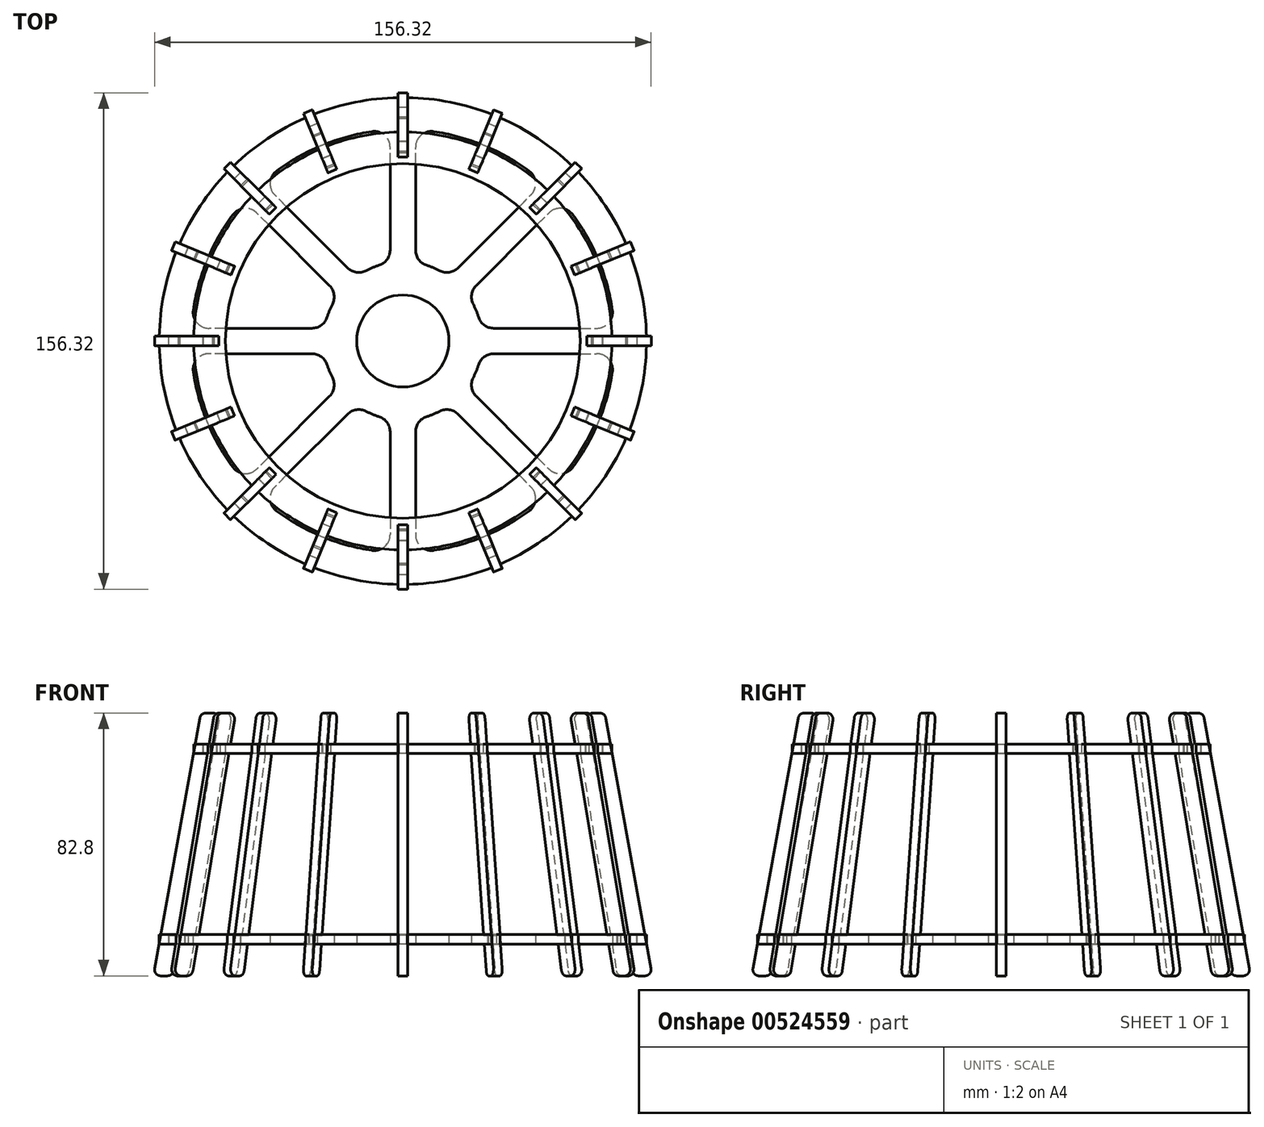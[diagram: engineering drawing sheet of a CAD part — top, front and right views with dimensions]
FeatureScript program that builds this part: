
annotation { "Feature Type Name" : "Feature", "Feature Type Description" : "" }
export const myFeature = defineFeature(function(context is Context, id is Id, definition is map)
    precondition{}
    {
        {
            var Q0;
            Q0=qCreatedBy(makeId("Top.planeOp"),FACE);
            cPlane(context, id + "F0", {"entities" : qUnion([Q0]), "cplaneType" : CPlaneType.OFFSET, "offset" : 60 * mm, "oppositeDirection" : true, "width" : 150 * mm, "height" : 150 * mm});
        }
        {
            var Q0;
            Q0=qCreatedBy(makeId("Top.planeOp"),FACE);
            var sketch = newSketch(context, id + "F1", { "sketchPlane" : qUnion([Q0])});
            skCircle(sketch, "E0", {"center": v(0, 0) * mm, "radius": 55.83 * mm});
            skArc(sketch, "E1", {"start": v(-65.82, -1.4) * mm, "mid": v(-64.57, -12.84) * mm, "end": v(-61.34, -23.9) * mm});
            skLineSegment(sketch, "E2", {"start": v(-65.82, 1.4) * mm, "end": v(-62.82, 1.4) * mm});
            skLineSegment(sketch, "E3", {"start": v(-62.82, 1.4) * mm, "end": v(-62.82, -1.4) * mm});
            skLineSegment(sketch, "E4", {"start": v(-62.82, -1.4) * mm, "end": v(-65.82, -1.4) * mm});
            skLineSegment(sketch, "E5.1.0", {"start": v(-61.34, -23.9) * mm, "end": v(-58.57, -22.75) * mm});
            skLineSegment(sketch, "E5.1.1", {"start": v(-58.57, -22.75) * mm, "end": v(-57.5, -25.33) * mm});
            skLineSegment(sketch, "E5.1.2", {"start": v(-57.5, -25.33) * mm, "end": v(-60.27, -26.48) * mm});
            skLineSegment(sketch, "E5.2.0", {"start": v(-47.53, -45.55) * mm, "end": v(-45.4, -43.43) * mm});
            skLineSegment(sketch, "E5.2.1", {"start": v(-45.4, -43.43) * mm, "end": v(-43.43, -45.4) * mm});
            skLineSegment(sketch, "E5.2.2", {"start": v(-43.43, -45.4) * mm, "end": v(-45.55, -47.53) * mm});
            skLineSegment(sketch, "E5.3.0", {"start": v(-26.48, -60.27) * mm, "end": v(-25.33, -57.5) * mm});
            skLineSegment(sketch, "E5.3.1", {"start": v(-25.33, -57.5) * mm, "end": v(-22.75, -58.57) * mm});
            skLineSegment(sketch, "E5.3.2", {"start": v(-22.75, -58.57) * mm, "end": v(-23.9, -61.34) * mm});
            skLineSegment(sketch, "E5.4.0", {"start": v(-1.4, -65.82) * mm, "end": v(-1.4, -62.82) * mm});
            skLineSegment(sketch, "E5.4.1", {"start": v(-1.4, -62.82) * mm, "end": v(1.4, -62.82) * mm});
            skLineSegment(sketch, "E5.4.2", {"start": v(1.4, -62.82) * mm, "end": v(1.4, -65.82) * mm});
            skLineSegment(sketch, "E5.5.0", {"start": v(23.9, -61.34) * mm, "end": v(22.75, -58.57) * mm});
            skLineSegment(sketch, "E5.5.1", {"start": v(22.75, -58.57) * mm, "end": v(25.33, -57.5) * mm});
            skLineSegment(sketch, "E5.5.2", {"start": v(25.33, -57.5) * mm, "end": v(26.48, -60.27) * mm});
            skLineSegment(sketch, "E5.6.0", {"start": v(45.55, -47.53) * mm, "end": v(43.43, -45.4) * mm});
            skLineSegment(sketch, "E5.6.1", {"start": v(43.43, -45.4) * mm, "end": v(45.4, -43.43) * mm});
            skLineSegment(sketch, "E5.6.2", {"start": v(45.4, -43.43) * mm, "end": v(47.53, -45.55) * mm});
            skLineSegment(sketch, "E5.7.0", {"start": v(60.27, -26.48) * mm, "end": v(57.5, -25.33) * mm});
            skLineSegment(sketch, "E5.7.1", {"start": v(57.5, -25.33) * mm, "end": v(58.57, -22.75) * mm});
            skLineSegment(sketch, "E5.7.2", {"start": v(58.57, -22.75) * mm, "end": v(61.34, -23.9) * mm});
            skLineSegment(sketch, "E5.8.0", {"start": v(65.82, -1.4) * mm, "end": v(62.82, -1.4) * mm});
            skLineSegment(sketch, "E5.8.1", {"start": v(62.82, -1.4) * mm, "end": v(62.82, 1.4) * mm});
            skLineSegment(sketch, "E5.8.2", {"start": v(62.82, 1.4) * mm, "end": v(65.82, 1.4) * mm});
            skLineSegment(sketch, "E5.9.0", {"start": v(61.34, 23.9) * mm, "end": v(58.57, 22.75) * mm});
            skLineSegment(sketch, "E5.9.1", {"start": v(58.57, 22.75) * mm, "end": v(57.5, 25.33) * mm});
            skLineSegment(sketch, "E5.9.2", {"start": v(57.5, 25.33) * mm, "end": v(60.27, 26.48) * mm});
            skLineSegment(sketch, "E5.10.0", {"start": v(47.53, 45.55) * mm, "end": v(45.4, 43.43) * mm});
            skLineSegment(sketch, "E5.10.1", {"start": v(45.4, 43.43) * mm, "end": v(43.43, 45.4) * mm});
            skLineSegment(sketch, "E5.10.2", {"start": v(43.43, 45.4) * mm, "end": v(45.55, 47.53) * mm});
            skLineSegment(sketch, "E5.11.0", {"start": v(26.48, 60.27) * mm, "end": v(25.33, 57.5) * mm});
            skLineSegment(sketch, "E5.11.1", {"start": v(25.33, 57.5) * mm, "end": v(22.75, 58.57) * mm});
            skLineSegment(sketch, "E5.11.2", {"start": v(22.75, 58.57) * mm, "end": v(23.9, 61.34) * mm});
            skLineSegment(sketch, "E5.12.0", {"start": v(1.4, 65.82) * mm, "end": v(1.4, 62.82) * mm});
            skLineSegment(sketch, "E5.12.1", {"start": v(1.4, 62.82) * mm, "end": v(-1.4, 62.82) * mm});
            skLineSegment(sketch, "E5.12.2", {"start": v(-1.4, 62.82) * mm, "end": v(-1.4, 65.82) * mm});
            skLineSegment(sketch, "E5.13.0", {"start": v(-23.9, 61.34) * mm, "end": v(-22.75, 58.57) * mm});
            skLineSegment(sketch, "E5.13.1", {"start": v(-22.75, 58.57) * mm, "end": v(-25.33, 57.5) * mm});
            skLineSegment(sketch, "E5.13.2", {"start": v(-25.33, 57.5) * mm, "end": v(-26.48, 60.27) * mm});
            skLineSegment(sketch, "E5.14.0", {"start": v(-45.55, 47.53) * mm, "end": v(-43.43, 45.4) * mm});
            skLineSegment(sketch, "E5.14.1", {"start": v(-43.43, 45.4) * mm, "end": v(-45.4, 43.43) * mm});
            skLineSegment(sketch, "E5.14.2", {"start": v(-45.4, 43.43) * mm, "end": v(-47.53, 45.55) * mm});
            skLineSegment(sketch, "E5.15.0", {"start": v(-60.27, 26.48) * mm, "end": v(-57.5, 25.33) * mm});
            skLineSegment(sketch, "E5.15.1", {"start": v(-57.5, 25.33) * mm, "end": v(-58.57, 22.75) * mm});
            skLineSegment(sketch, "E5.15.2", {"start": v(-58.57, 22.75) * mm, "end": v(-61.34, 23.9) * mm});
            skArc(sketch, "E6.trimOffspring", {"start": v(-61.34, 23.9) * mm, "mid": v(-64.57, 12.84) * mm, "end": v(-65.82, 1.4) * mm});
            skArc(sketch, "E7.trimOffspring", {"start": v(-47.53, 45.55) * mm, "mid": v(-54.74, 36.57) * mm, "end": v(-60.27, 26.48) * mm});
            skArc(sketch, "E8.trimOffspring", {"start": v(-26.48, 60.27) * mm, "mid": v(-36.57, 54.74) * mm, "end": v(-45.55, 47.53) * mm});
            skArc(sketch, "E9.trimOffspring", {"start": v(-1.4, 65.82) * mm, "mid": v(-12.84, 64.57) * mm, "end": v(-23.9, 61.34) * mm});
            skArc(sketch, "E10.trimOffspring", {"start": v(23.9, 61.34) * mm, "mid": v(12.84, 64.57) * mm, "end": v(1.4, 65.82) * mm});
            skArc(sketch, "E11.trimOffspring", {"start": v(45.55, 47.53) * mm, "mid": v(36.57, 54.74) * mm, "end": v(26.48, 60.27) * mm});
            skArc(sketch, "E12.trimOffspring", {"start": v(60.27, 26.48) * mm, "mid": v(54.74, 36.57) * mm, "end": v(47.53, 45.55) * mm});
            skArc(sketch, "E13.trimOffspring", {"start": v(65.82, 1.4) * mm, "mid": v(64.57, 12.84) * mm, "end": v(61.34, 23.9) * mm});
            skArc(sketch, "E14.trimOffspring", {"start": v(61.34, -23.9) * mm, "mid": v(64.57, -12.84) * mm, "end": v(65.82, -1.4) * mm});
            skArc(sketch, "E15.trimOffspring", {"start": v(47.53, -45.55) * mm, "mid": v(54.74, -36.57) * mm, "end": v(60.27, -26.48) * mm});
            skArc(sketch, "E16.trimOffspring", {"start": v(26.48, -60.27) * mm, "mid": v(36.57, -54.74) * mm, "end": v(45.55, -47.53) * mm});
            skArc(sketch, "E17.trimOffspring", {"start": v(1.4, -65.82) * mm, "mid": v(12.84, -64.57) * mm, "end": v(23.9, -61.34) * mm});
            skArc(sketch, "E18.trimOffspring", {"start": v(-23.9, -61.34) * mm, "mid": v(-12.84, -64.57) * mm, "end": v(-1.4, -65.82) * mm});
            skArc(sketch, "E19.trimOffspring", {"start": v(-45.55, -47.53) * mm, "mid": v(-36.57, -54.74) * mm, "end": v(-26.48, -60.27) * mm});
            skArc(sketch, "E20.trimOffspring", {"start": v(-60.27, -26.48) * mm, "mid": v(-54.74, -36.57) * mm, "end": v(-47.53, -45.55) * mm});
            skSolve(sketch);
        }
        {
            var Q0;
            Q0=qSketchRegion(id+"F1",true);
            extrude(context, id + "F2", {"entities" : qUnion([Q0]), "depth" : 3 * mm});
        }
        {
            var Q0;
            Q0=qCreatedBy(id+"F0.planeOp",FACE);
            var sketch = newSketch(context, id + "F3", { "sketchPlane" : qUnion([Q0])});
            skArc(sketch, "E21", {"start": v(-9.73, 65.95) * mm, "mid": v(-25.51, 61.6) * mm, "end": v(-39.76, 53.52) * mm});
            skArc(sketch, "E22", {"start": v(-76.65, -1.4) * mm, "mid": v(-75.2, -14.96) * mm, "end": v(-71.36, -28.04) * mm});
            skArc(sketch, "E23.trimOffspring", {"start": v(-71.36, 28.04) * mm, "mid": v(-75.2, 14.96) * mm, "end": v(-76.65, 1.4) * mm});
            skArc(sketch, "E24.trimOffspring", {"start": v(-55.2, 53.21) * mm, "mid": v(-63.75, 42.6) * mm, "end": v(-70.28, 30.63) * mm});
            skArc(sketch, "E25.trimOffspring", {"start": v(-30.63, 70.28) * mm, "mid": v(-42.6, 63.75) * mm, "end": v(-53.21, 55.2) * mm});
            skArc(sketch, "E26.trimOffspring", {"start": v(-1.4, 76.65) * mm, "mid": v(-14.96, 75.2) * mm, "end": v(-28.04, 71.36) * mm});
            skArc(sketch, "E27.trimOffspring", {"start": v(28.04, 71.36) * mm, "mid": v(14.96, 75.2) * mm, "end": v(1.4, 76.65) * mm});
            skArc(sketch, "E28.trimOffspring", {"start": v(53.21, 55.2) * mm, "mid": v(42.6, 63.75) * mm, "end": v(30.63, 70.28) * mm});
            skArc(sketch, "E29.trimOffspring", {"start": v(70.28, 30.63) * mm, "mid": v(63.75, 42.6) * mm, "end": v(55.2, 53.21) * mm});
            skArc(sketch, "E30.trimOffspring", {"start": v(76.65, 1.4) * mm, "mid": v(75.2, 14.96) * mm, "end": v(71.36, 28.04) * mm});
            skArc(sketch, "E31.trimOffspring", {"start": v(71.36, -28.04) * mm, "mid": v(75.2, -14.96) * mm, "end": v(76.65, -1.4) * mm});
            skArc(sketch, "E32.trimOffspring", {"start": v(55.2, -53.21) * mm, "mid": v(63.75, -42.6) * mm, "end": v(70.28, -30.63) * mm});
            skArc(sketch, "E33.trimOffspring", {"start": v(30.63, -70.28) * mm, "mid": v(42.6, -63.75) * mm, "end": v(53.21, -55.2) * mm});
            skArc(sketch, "E34.trimOffspring", {"start": v(1.4, -76.65) * mm, "mid": v(14.96, -75.2) * mm, "end": v(28.04, -71.36) * mm});
            skArc(sketch, "E35.trimOffspring", {"start": v(-28.04, -71.36) * mm, "mid": v(-14.96, -75.2) * mm, "end": v(-1.4, -76.65) * mm});
            skArc(sketch, "E36.trimOffspring", {"start": v(-53.21, -55.2) * mm, "mid": v(-42.6, -63.75) * mm, "end": v(-30.63, -70.28) * mm});
            skArc(sketch, "E37.trimOffspring", {"start": v(-70.28, -30.63) * mm, "mid": v(-63.75, -42.6) * mm, "end": v(-55.2, -53.21) * mm});
            skLineSegment(sketch, "E38", {"start": v(-76.65, -1.4) * mm, "end": v(-73.65, -1.4) * mm});
            skLineSegment(sketch, "E39", {"start": v(-73.65, -1.4) * mm, "end": v(-73.65, 1.4) * mm});
            skLineSegment(sketch, "E40", {"start": v(-76.65, 1.4) * mm, "end": v(-73.65, 1.4) * mm});
            skLineSegment(sketch, "E41.1.0", {"start": v(-71.36, -28.04) * mm, "end": v(-68.58, -26.9) * mm});
            skLineSegment(sketch, "E41.1.1", {"start": v(-67.51, -29.48) * mm, "end": v(-68.58, -26.9) * mm});
            skLineSegment(sketch, "E41.1.2", {"start": v(-70.28, -30.63) * mm, "end": v(-67.51, -29.48) * mm});
            skLineSegment(sketch, "E41.2.0", {"start": v(-55.2, -53.21) * mm, "end": v(-53.07, -51.1) * mm});
            skLineSegment(sketch, "E41.2.1", {"start": v(-51.1, -53.07) * mm, "end": v(-53.07, -51.1) * mm});
            skLineSegment(sketch, "E41.2.2", {"start": v(-53.21, -55.2) * mm, "end": v(-51.1, -53.07) * mm});
            skLineSegment(sketch, "E41.3.0", {"start": v(-30.63, -70.28) * mm, "end": v(-29.48, -67.51) * mm});
            skLineSegment(sketch, "E41.3.1", {"start": v(-26.9, -68.58) * mm, "end": v(-29.48, -67.51) * mm});
            skLineSegment(sketch, "E41.3.2", {"start": v(-28.04, -71.36) * mm, "end": v(-26.9, -68.58) * mm});
            skLineSegment(sketch, "E41.4.0", {"start": v(-1.4, -76.65) * mm, "end": v(-1.4, -73.65) * mm});
            skLineSegment(sketch, "E41.4.1", {"start": v(1.4, -73.65) * mm, "end": v(-1.4, -73.65) * mm});
            skLineSegment(sketch, "E41.4.2", {"start": v(1.4, -76.65) * mm, "end": v(1.4, -73.65) * mm});
            skLineSegment(sketch, "E41.5.0", {"start": v(28.04, -71.36) * mm, "end": v(26.9, -68.58) * mm});
            skLineSegment(sketch, "E41.5.1", {"start": v(29.48, -67.51) * mm, "end": v(26.9, -68.58) * mm});
            skLineSegment(sketch, "E41.5.2", {"start": v(30.63, -70.28) * mm, "end": v(29.48, -67.51) * mm});
            skLineSegment(sketch, "E41.6.0", {"start": v(53.21, -55.2) * mm, "end": v(51.1, -53.07) * mm});
            skLineSegment(sketch, "E41.6.1", {"start": v(53.07, -51.1) * mm, "end": v(51.1, -53.07) * mm});
            skLineSegment(sketch, "E41.6.2", {"start": v(55.2, -53.21) * mm, "end": v(53.07, -51.1) * mm});
            skLineSegment(sketch, "E41.7.0", {"start": v(70.28, -30.63) * mm, "end": v(67.51, -29.48) * mm});
            skLineSegment(sketch, "E41.7.1", {"start": v(68.58, -26.9) * mm, "end": v(67.51, -29.48) * mm});
            skLineSegment(sketch, "E41.7.2", {"start": v(71.36, -28.04) * mm, "end": v(68.58, -26.9) * mm});
            skLineSegment(sketch, "E41.8.0", {"start": v(76.65, -1.4) * mm, "end": v(73.65, -1.4) * mm});
            skLineSegment(sketch, "E41.8.1", {"start": v(73.65, 1.4) * mm, "end": v(73.65, -1.4) * mm});
            skLineSegment(sketch, "E41.8.2", {"start": v(76.65, 1.4) * mm, "end": v(73.65, 1.4) * mm});
            skLineSegment(sketch, "E41.9.0", {"start": v(71.36, 28.04) * mm, "end": v(68.58, 26.9) * mm});
            skLineSegment(sketch, "E41.9.1", {"start": v(67.51, 29.48) * mm, "end": v(68.58, 26.9) * mm});
            skLineSegment(sketch, "E41.9.2", {"start": v(70.28, 30.63) * mm, "end": v(67.51, 29.48) * mm});
            skLineSegment(sketch, "E41.10.0", {"start": v(55.2, 53.21) * mm, "end": v(53.07, 51.1) * mm});
            skLineSegment(sketch, "E41.10.1", {"start": v(51.1, 53.07) * mm, "end": v(53.07, 51.1) * mm});
            skLineSegment(sketch, "E41.10.2", {"start": v(53.21, 55.2) * mm, "end": v(51.1, 53.07) * mm});
            skLineSegment(sketch, "E41.11.0", {"start": v(30.63, 70.28) * mm, "end": v(29.48, 67.51) * mm});
            skLineSegment(sketch, "E41.11.1", {"start": v(26.9, 68.58) * mm, "end": v(29.48, 67.51) * mm});
            skLineSegment(sketch, "E41.11.2", {"start": v(28.04, 71.36) * mm, "end": v(26.9, 68.58) * mm});
            skLineSegment(sketch, "E41.12.0", {"start": v(1.4, 76.65) * mm, "end": v(1.4, 73.65) * mm});
            skLineSegment(sketch, "E41.12.1", {"start": v(-1.4, 73.65) * mm, "end": v(1.4, 73.65) * mm});
            skLineSegment(sketch, "E41.12.2", {"start": v(-1.4, 76.65) * mm, "end": v(-1.4, 73.65) * mm});
            skLineSegment(sketch, "E41.13.0", {"start": v(-28.04, 71.36) * mm, "end": v(-26.9, 68.58) * mm});
            skLineSegment(sketch, "E41.13.1", {"start": v(-29.48, 67.51) * mm, "end": v(-26.9, 68.58) * mm});
            skLineSegment(sketch, "E41.13.2", {"start": v(-30.63, 70.28) * mm, "end": v(-29.48, 67.51) * mm});
            skLineSegment(sketch, "E41.14.0", {"start": v(-53.21, 55.2) * mm, "end": v(-51.1, 53.07) * mm});
            skLineSegment(sketch, "E41.14.1", {"start": v(-53.07, 51.1) * mm, "end": v(-51.1, 53.07) * mm});
            skLineSegment(sketch, "E41.14.2", {"start": v(-55.2, 53.21) * mm, "end": v(-53.07, 51.1) * mm});
            skLineSegment(sketch, "E41.15.0", {"start": v(-70.28, 30.63) * mm, "end": v(-67.51, 29.48) * mm});
            skLineSegment(sketch, "E41.15.1", {"start": v(-68.58, 26.9) * mm, "end": v(-67.51, 29.48) * mm});
            skLineSegment(sketch, "E41.15.2", {"start": v(-71.36, 28.04) * mm, "end": v(-68.58, 26.9) * mm});
            skCircle(sketch, "E42", {"center": v(0, 0) * mm, "radius": 14.5 * mm});
            skArc(sketch, "E43", {"start": v(-7.5, 23.85) * mm, "mid": v(-9.57, 23.1) * mm, "end": v(-11.56, 22.17) * mm});
            skLineSegment(sketch, "E44", {"start": v(-4, 28.62) * mm, "end": v(-4, 61) * mm});
            skLineSegment(sketch, "E45", {"start": v(4, 28.62) * mm, "end": v(4, 61) * mm});
            skPoint(sketch, "E46.visualSharp", {"position": v(-4, 24.68) * mm});
            skArc(sketch, "E46.filletArc", {"start": v(-7.5, 23.85) * mm, "mid": v(-4.97, 25.66) * mm, "end": v(-4, 28.62) * mm});
            skPoint(sketch, "E47.visualSharp", {"position": v(4, 24.68) * mm});
            skArc(sketch, "E47.filletArc", {"start": v(4, 28.62) * mm, "mid": v(4.97, 25.66) * mm, "end": v(7.5, 23.85) * mm});
            skPoint(sketch, "E48.visualSharp", {"position": v(4, 66.55) * mm});
            skArc(sketch, "E48.filletArc", {"start": v(9.73, 65.95) * mm, "mid": v(5.73, 64.8) * mm, "end": v(4, 61) * mm});
            skPoint(sketch, "E49.visualSharp", {"position": v(-4, 66.55) * mm});
            skArc(sketch, "E49.filletArc", {"start": v(-4, 61) * mm, "mid": v(-5.73, 64.8) * mm, "end": v(-9.73, 65.95) * mm});
            skArc(sketch, "E50.1.0", {"start": v(-39.76, 53.52) * mm, "mid": v(-41.76, 49.87) * mm, "end": v(-40.3, 45.97) * mm});
            skLineSegment(sketch, "E50.1.1", {"start": v(-17.4, 23.06) * mm, "end": v(-40.3, 45.97) * mm});
            skLineSegment(sketch, "E50.1.2", {"start": v(-23.06, 17.4) * mm, "end": v(-45.97, 40.3) * mm});
            skArc(sketch, "E50.1.3", {"start": v(-45.97, 40.3) * mm, "mid": v(-49.87, 41.76) * mm, "end": v(-53.52, 39.76) * mm});
            skArc(sketch, "E50.1.4", {"start": v(-22.17, 11.56) * mm, "mid": v(-21.66, 14.63) * mm, "end": v(-23.06, 17.4) * mm});
            skArc(sketch, "E50.1.5", {"start": v(-17.4, 23.06) * mm, "mid": v(-14.63, 21.66) * mm, "end": v(-11.56, 22.17) * mm});
            skArc(sketch, "E50.2.0", {"start": v(-65.95, 9.73) * mm, "mid": v(-64.8, 5.73) * mm, "end": v(-61, 4) * mm});
            skLineSegment(sketch, "E50.2.1", {"start": v(-28.62, 4) * mm, "end": v(-61, 4) * mm});
            skLineSegment(sketch, "E50.2.2", {"start": v(-28.62, -4) * mm, "end": v(-61, -4) * mm});
            skArc(sketch, "E50.2.3", {"start": v(-61, -4) * mm, "mid": v(-64.8, -5.73) * mm, "end": v(-65.95, -9.73) * mm});
            skArc(sketch, "E50.2.4", {"start": v(-23.85, -7.5) * mm, "mid": v(-25.66, -4.97) * mm, "end": v(-28.62, -4) * mm});
            skArc(sketch, "E50.2.5", {"start": v(-28.62, 4) * mm, "mid": v(-25.66, 4.97) * mm, "end": v(-23.85, 7.5) * mm});
            skArc(sketch, "E50.3.0", {"start": v(-53.52, -39.76) * mm, "mid": v(-49.87, -41.76) * mm, "end": v(-45.97, -40.3) * mm});
            skLineSegment(sketch, "E50.3.1", {"start": v(-23.06, -17.4) * mm, "end": v(-45.97, -40.3) * mm});
            skLineSegment(sketch, "E50.3.2", {"start": v(-17.4, -23.06) * mm, "end": v(-40.3, -45.97) * mm});
            skArc(sketch, "E50.3.3", {"start": v(-40.3, -45.97) * mm, "mid": v(-41.76, -49.87) * mm, "end": v(-39.76, -53.52) * mm});
            skArc(sketch, "E50.3.4", {"start": v(-11.56, -22.17) * mm, "mid": v(-14.63, -21.66) * mm, "end": v(-17.4, -23.06) * mm});
            skArc(sketch, "E50.3.5", {"start": v(-23.06, -17.4) * mm, "mid": v(-21.66, -14.63) * mm, "end": v(-22.17, -11.56) * mm});
            skLineSegment(sketch, "E51.4.4.0", {"start": v(-4, -28.62) * mm, "end": v(-4, -61) * mm});
            skLineSegment(sketch, "E51.7.4.0", {"start": v(4, -28.62) * mm, "end": v(4, -61) * mm});
            skArc(sketch, "E51.10.4.0", {"start": v(4, -61) * mm, "mid": v(5.73, -64.8) * mm, "end": v(9.73, -65.95) * mm});
            skArc(sketch, "E51.14.4.0", {"start": v(7.5, -23.85) * mm, "mid": v(4.97, -25.66) * mm, "end": v(4, -28.62) * mm});
            skArc(sketch, "E51.16.4.0", {"start": v(-9.73, -65.95) * mm, "mid": v(-5.73, -64.8) * mm, "end": v(-4, -61) * mm});
            skArc(sketch, "E51.18.4.0", {"start": v(-4, -28.62) * mm, "mid": v(-4.97, -25.66) * mm, "end": v(-7.5, -23.85) * mm});
            skLineSegment(sketch, "E51.4.5.0", {"start": v(17.4, -23.06) * mm, "end": v(40.3, -45.97) * mm});
            skLineSegment(sketch, "E51.7.5.0", {"start": v(23.06, -17.4) * mm, "end": v(45.97, -40.3) * mm});
            skArc(sketch, "E51.10.5.0", {"start": v(45.97, -40.3) * mm, "mid": v(49.87, -41.76) * mm, "end": v(53.52, -39.76) * mm});
            skArc(sketch, "E51.14.5.0", {"start": v(22.17, -11.56) * mm, "mid": v(21.66, -14.63) * mm, "end": v(23.06, -17.4) * mm});
            skArc(sketch, "E51.16.5.0", {"start": v(39.76, -53.52) * mm, "mid": v(41.76, -49.87) * mm, "end": v(40.3, -45.97) * mm});
            skArc(sketch, "E51.18.5.0", {"start": v(17.4, -23.06) * mm, "mid": v(14.63, -21.66) * mm, "end": v(11.56, -22.17) * mm});
            skLineSegment(sketch, "E52.4.6.0", {"start": v(28.62, -4) * mm, "end": v(61, -4) * mm});
            skLineSegment(sketch, "E52.7.6.0", {"start": v(28.62, 4) * mm, "end": v(61, 4) * mm});
            skArc(sketch, "E52.10.6.0", {"start": v(61, 4) * mm, "mid": v(64.8, 5.73) * mm, "end": v(65.95, 9.73) * mm});
            skArc(sketch, "E52.14.6.0", {"start": v(23.85, 7.5) * mm, "mid": v(25.66, 4.97) * mm, "end": v(28.62, 4) * mm});
            skArc(sketch, "E52.16.6.0", {"start": v(65.95, -9.73) * mm, "mid": v(64.8, -5.73) * mm, "end": v(61, -4) * mm});
            skArc(sketch, "E52.18.6.0", {"start": v(28.62, -4) * mm, "mid": v(25.66, -4.97) * mm, "end": v(23.85, -7.5) * mm});
            skLineSegment(sketch, "E52.4.7.0", {"start": v(23.06, 17.4) * mm, "end": v(45.97, 40.3) * mm});
            skLineSegment(sketch, "E52.7.7.0", {"start": v(17.4, 23.06) * mm, "end": v(40.3, 45.97) * mm});
            skArc(sketch, "E52.10.7.0", {"start": v(40.3, 45.97) * mm, "mid": v(41.76, 49.87) * mm, "end": v(39.76, 53.52) * mm});
            skArc(sketch, "E52.14.7.0", {"start": v(11.56, 22.17) * mm, "mid": v(14.63, 21.66) * mm, "end": v(17.4, 23.06) * mm});
            skArc(sketch, "E52.16.7.0", {"start": v(53.52, 39.76) * mm, "mid": v(49.87, 41.76) * mm, "end": v(45.97, 40.3) * mm});
            skArc(sketch, "E52.18.7.0", {"start": v(23.06, 17.4) * mm, "mid": v(21.66, 14.63) * mm, "end": v(22.17, 11.56) * mm});
            skArc(sketch, "E53.trimOffspring", {"start": v(-53.52, 39.76) * mm, "mid": v(-61.6, 25.51) * mm, "end": v(-65.95, 9.73) * mm});
            skArc(sketch, "E54.trimOffspring", {"start": v(-22.17, 11.56) * mm, "mid": v(-23.1, 9.57) * mm, "end": v(-23.85, 7.5) * mm});
            skArc(sketch, "E55.trimOffspring", {"start": v(-23.85, -7.5) * mm, "mid": v(-23.1, -9.57) * mm, "end": v(-22.17, -11.56) * mm});
            skArc(sketch, "E56.trimOffspring", {"start": v(11.56, 22.17) * mm, "mid": v(9.57, 23.1) * mm, "end": v(7.5, 23.85) * mm});
            skArc(sketch, "E57.trimOffspring", {"start": v(23.85, 7.5) * mm, "mid": v(23.1, 9.57) * mm, "end": v(22.17, 11.56) * mm});
            skArc(sketch, "E58.trimOffspring", {"start": v(22.17, -11.56) * mm, "mid": v(23.1, -9.57) * mm, "end": v(23.85, -7.5) * mm});
            skArc(sketch, "E59.trimOffspring", {"start": v(7.5, -23.85) * mm, "mid": v(9.57, -23.1) * mm, "end": v(11.56, -22.17) * mm});
            skArc(sketch, "E60.trimOffspring", {"start": v(-11.56, -22.17) * mm, "mid": v(-9.57, -23.1) * mm, "end": v(-7.5, -23.85) * mm});
            skArc(sketch, "E61.trimOffspring", {"start": v(-39.76, -53.52) * mm, "mid": v(-25.51, -61.6) * mm, "end": v(-9.73, -65.95) * mm});
            skArc(sketch, "E62.trimOffspring", {"start": v(9.73, -65.95) * mm, "mid": v(25.51, -61.6) * mm, "end": v(39.76, -53.52) * mm});
            skArc(sketch, "E63.trimOffspring", {"start": v(-65.95, -9.73) * mm, "mid": v(-61.6, -25.51) * mm, "end": v(-53.52, -39.76) * mm});
            skArc(sketch, "E64.trimOffspring", {"start": v(39.76, 53.52) * mm, "mid": v(25.51, 61.6) * mm, "end": v(9.73, 65.95) * mm});
            skArc(sketch, "E65.trimOffspring", {"start": v(65.95, 9.73) * mm, "mid": v(61.6, 25.51) * mm, "end": v(53.52, 39.76) * mm});
            skArc(sketch, "E66.trimOffspring", {"start": v(53.52, -39.76) * mm, "mid": v(61.6, -25.51) * mm, "end": v(65.95, -9.73) * mm});
            skSolve(sketch);
        }
        {
            var Q0;
            Q0=qSketchRegion(id+"F3",true);
            extrude(context, id + "F4", {"entities" : qUnion([Q0]), "depth" : 3 * mm});
        }
        {
            var Q0;
            Q0=qCreatedBy(makeId("Front.planeOp"),FACE);
            var sketch = newSketch(context, id + "F5", { "sketchPlane" : qUnion([Q0])});
            skLineSegment(sketch, "E67", {"start": v(-57.94, 10.44) * mm, "end": v(-59.32, 2.8) * mm});
            skLineSegment(sketch, "E68", {"start": v(-63.9, 11.16) * mm, "end": v(-78.13, -67.64) * mm});
            skLineSegment(sketch, "E69", {"start": v(-59.82, 0) * mm, "end": v(-62.82, 0) * mm});
            skLineSegment(sketch, "E70", {"start": v(-62.82, 0) * mm, "end": v(-62.82, 2.8) * mm});
            skLineSegment(sketch, "E71", {"start": v(-62.82, 2.8) * mm, "end": v(-59.32, 2.8) * mm});
            skLineSegment(sketch, "E72.trimOffspring", {"start": v(-59.82, 0) * mm, "end": v(-70.15, -57.2) * mm});
            skLineSegment(sketch, "E73", {"start": v(-70.65, -60) * mm, "end": v(-73.65, -60) * mm});
            skLineSegment(sketch, "E74", {"start": v(-73.65, -60) * mm, "end": v(-73.65, -57.2) * mm});
            skLineSegment(sketch, "E75", {"start": v(-73.65, -57.2) * mm, "end": v(-70.15, -57.2) * mm});
            skLineSegment(sketch, "E76.trimOffspring", {"start": v(-70.65, -60) * mm, "end": v(-72.16, -68.36) * mm});
            skLineSegment(sketch, "E77", {"start": v(-59.9, 12.8) * mm, "end": v(-61.94, 12.8) * mm});
            skPoint(sketch, "E78.visualSharp", {"position": v(-63.6, 12.8) * mm});
            skArc(sketch, "E78.filletArc", {"start": v(-61.94, 12.8) * mm, "mid": v(-63.22, 12.33) * mm, "end": v(-63.9, 11.16) * mm});
            skPoint(sketch, "E79.visualSharp", {"position": v(-57.5, 12.8) * mm});
            skArc(sketch, "E79.filletArc", {"start": v(-57.94, 10.44) * mm, "mid": v(-58.37, 12.08) * mm, "end": v(-59.9, 12.8) * mm});
            skLineSegment(sketch, "E80", {"start": v(-74.13, -70) * mm, "end": v(-76.16, -70) * mm});
            skPoint(sketch, "E81.visualSharp", {"position": v(-78.56, -70) * mm});
            skArc(sketch, "E81.filletArc", {"start": v(-78.13, -67.64) * mm, "mid": v(-77.7, -69.28) * mm, "end": v(-76.16, -70) * mm});
            skPoint(sketch, "E82.visualSharp", {"position": v(-72.46, -70) * mm});
            skArc(sketch, "E82.filletArc", {"start": v(-74.13, -70) * mm, "mid": v(-72.85, -69.53) * mm, "end": v(-72.16, -68.36) * mm});
            skSolve(sketch);
        }
        {
            var Q0;
            Q0=qSketchRegion(id+"F5",true);
            extrude(context, id + "F6", {"entities" : qUnion([Q0]), "endBound" : BoundingType.SYMMETRIC, "depth" : 3 * mm});
        }
        {
            var Q0;
            Q0=makeQuery(id+"F6.opExtrude","SWEPT_BODY",BODY,{"disambiguationData":[OSD([sQuery(id+"F5.wireOp",EDGE,"E67"),sQuery(id+"F5.wireOp",EDGE,"E68"),sQuery(id+"F5.wireOp",EDGE,"E69"),sQuery(id+"F5.wireOp",EDGE,"E70"),sQuery(id+"F5.wireOp",EDGE,"E71"),sQuery(id+"F5.wireOp",EDGE,"E72.trimOffspring"),sQuery(id+"F5.wireOp",EDGE,"E73"),sQuery(id+"F5.wireOp",EDGE,"E74"),sQuery(id+"F5.wireOp",EDGE,"E75"),sQuery(id+"F5.wireOp",EDGE,"E76.trimOffspring"),sQuery(id+"F5.wireOp",EDGE,"E77"),sQuery(id+"F5.wireOp",EDGE,"E78.filletArc"),sQuery(id+"F5.wireOp",EDGE,"E79.filletArc"),sQuery(id+"F5.wireOp",EDGE,"E80"),sQuery(id+"F5.wireOp",EDGE,"E81.filletArc"),sQuery(id+"F5.wireOp",EDGE,"E82.filletArc")])]});
            var Q1;
            Q1=sQuery(id+"F1.wireOp",EDGE,"E0");
            circularPattern(context, id + "F7", {"entities" : qUnion([Q0]), "axis" : qUnion([Q1]), "angle" : 360 * degree, "instanceCount" : 16, "equalSpace" : true});
        }
    });
